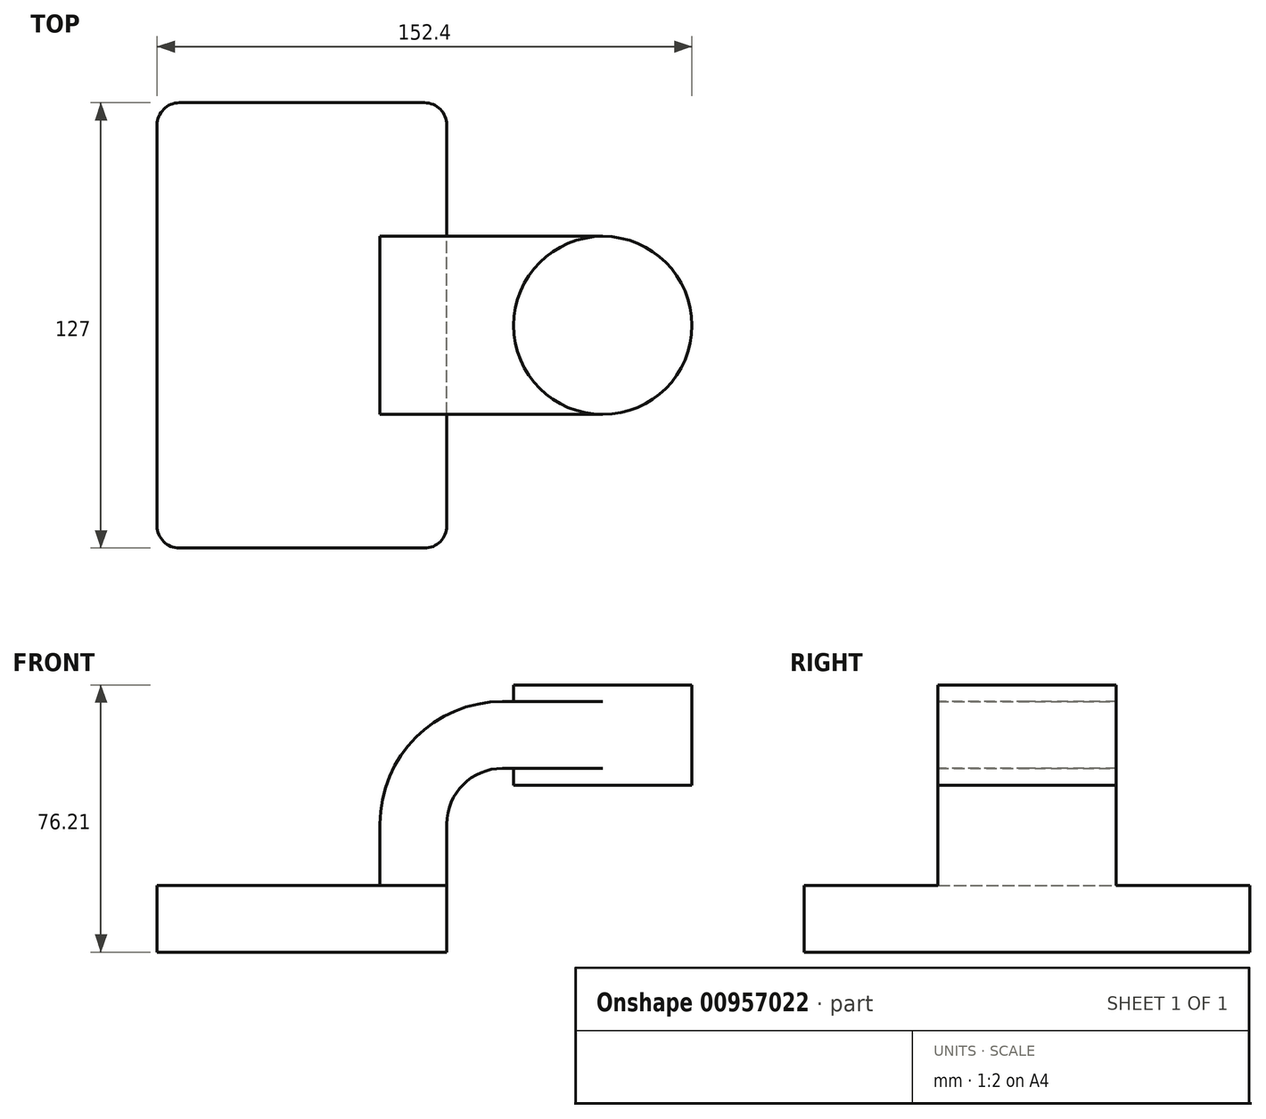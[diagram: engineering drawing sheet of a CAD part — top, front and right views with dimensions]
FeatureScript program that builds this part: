
annotation { "Feature Type Name" : "Feature", "Feature Type Description" : "" }
export const myFeature = defineFeature(function(context is Context, id is Id, definition is map)
    precondition{}
    {
        {
            var Q0;
            Q0=qCreatedBy(makeId("Front.planeOp"),FACE);
            var sketch = newSketch(context, id + "F0", { "sketchPlane" : qUnion([Q0])});
            skLineSegment(sketch, "E0.bottom", {"start": v(41.27, 9.52) * mm, "end": v(-41.28, 9.52) * mm});
            skLineSegment(sketch, "E0.top", {"start": v(41.28, -9.53) * mm, "end": v(-41.27, -9.53) * mm});
            skLineSegment(sketch, "E0.left", {"start": v(41.28, 9.53) * mm, "end": v(41.28, -9.52) * mm});
            skLineSegment(sketch, "E0.right", {"start": v(-41.27, 9.53) * mm, "end": v(-41.27, -9.52) * mm});
            skPoint(sketch, "E0.middle", {"position": v(0, 0) * mm});
            skLineSegment(sketch, "E1.bottom", {"start": v(111.12, 38.1) * mm, "end": v(60.32, 38.1) * mm});
            skLineSegment(sketch, "E1.top", {"start": v(111.12, 66.68) * mm, "end": v(60.33, 66.68) * mm});
            skLineSegment(sketch, "E1.left", {"start": v(111.12, 38.1) * mm, "end": v(111.12, 66.68) * mm});
            skLineSegment(sketch, "E1.right", {"start": v(60.32, 38.1) * mm, "end": v(60.32, 66.68) * mm});
            skPoint(sketch, "E1.middle", {"position": v(85.72, 52.39) * mm});
            skLineSegment(sketch, "E2", {"start": v(41.28, 9.53) * mm, "end": v(41.28, 27) * mm});
            skArc(sketch, "E3", {"start": v(41.27, 27) * mm, "mid": v(45.92, 38.23) * mm, "end": v(57.15, 42.88) * mm});
            skLineSegment(sketch, "E4", {"start": v(57.15, 42.88) * mm, "end": v(85.72, 42.88) * mm});
            skLineSegment(sketch, "E5.0", {"start": v(57.15, 61.93) * mm, "end": v(85.72, 61.93) * mm});
            skArc(sketch, "E5.1", {"start": v(22.23, 27) * mm, "mid": v(32.45, 51.7) * mm, "end": v(57.15, 61.93) * mm});
            skLineSegment(sketch, "E5.2", {"start": v(22.22, 9.53) * mm, "end": v(22.22, 27) * mm});
            skFitSpline(sketch, "E6", {"points": [v(-41.27, 9.53) * mm, v(57.15, 61.93) * mm], "startDerivative": vector(2.15, 157.2) * mm, "endDerivative": vector(50.04, 0) * mm});
            skLineSegment(sketch, "E7", {"start": v(85.72, 38.1) * mm, "end": v(85.72, 66.68) * mm});
            skSolve(sketch);
        }
        {
            var Q0;
            Q0=makeQuery(id+"F0.imprint","IMPRINT",FACE,{"disambiguationData":[TD([[makeQuery(id+"F0.imprint","IMPRINT",EDGE,{"derivedFrom":sQuery(id+"F0.wireOp",EDGE,"E0.top")}),-1.0]])]});
            extrude(context, id + "F1", {"entities" : qUnion([Q0]), "endBound" : BoundingType.SYMMETRIC, "depth" : 127 * mm, "offsetDistance" : 25.4 * mm});
        }
        {
            var Q0;
            {var subQ1=sQuery(id+"F0.wireOp",EDGE,"E2");Q0=makeQuery(id+"F0.imprint","IMPRINT",FACE,{"disambiguationData":[TD([[makeQuery(id+"F0.imprint","IMPRINT",EDGE,{"derivedFrom":subQ1}),1.0]])]});}
            var Q1;
            {var subQ0=sQuery(id+"F0.wireOp",EDGE,"E4");var subQ1=sQuery(id+"F0.wireOp",EDGE,"E1.right");var subQ2=makeQuery(id+"F0.imprint","INTERSECT",VERTEX,{"derivedFrom":[subQ1,subQ0]});Q1=makeQuery(id+"F0.imprint","IMPRINT",FACE,{"disambiguationData":[TD([[makeQuery(id+"F0.imprint","IMPRINT",EDGE,{"disambiguationData":[TD([[subQ2,-1.0]])],"derivedFrom":subQ1}),-1.0]])]});}
            extrude(context, id + "F2", {"entities" : qUnion([Q0, Q1]), "operationType" : NewBodyOperationType.ADD, "endBound" : BoundingType.SYMMETRIC, "depth" : 50.8 * mm, "offsetDistance" : 25.4 * mm});
        }
        {
            var Q0;
            Q0=makeQuery(id+"F0.imprint","IMPRINT",FACE,{"disambiguationData":[TD([[makeQuery(id+"F0.imprint","IMPRINT",EDGE,{"derivedFrom":sQuery(id+"F0.wireOp",EDGE,"E5.1")}),1.0]])]});
            extrude(context, id + "F3", {"entities" : qUnion([Q0]), "operationType" : NewBodyOperationType.ADD, "endBound" : BoundingType.SYMMETRIC, "depth" : 15.88 * mm, "offsetDistance" : 25.4 * mm});
        }
        {
            var Q0;
            {var subQ0=sQuery(id+"F0.wireOp",EDGE,"E1.left");Q0=makeQuery(id+"F0.imprint","IMPRINT",FACE,{"disambiguationData":[TD([[makeQuery(id+"F0.imprint","IMPRINT",EDGE,{"derivedFrom":subQ0}),1.0]])]});}
            var Q1;
            Q1=sQuery(id+"F0.wireOp",EDGE,"E7");
            revolve(context, id + "F4", {"operationType" : NewBodyOperationType.ADD, "surfaceOperationType" : NewSurfaceOperationType.NEW, "entities" : qUnion([Q0]), "axis" : qUnion([Q1]), "revolveType" : RevolveType.FULL});
        }
        {
            var Q0;
            Q0=makeQuery(id+"F1.opExtrude","CAP_EDGE",EDGE,{"disambiguationData":[OSD([sQuery(id+"F0.wireOp",EDGE,"E0.right")])],"isStart":false});
            var Q1;
            Q1=makeQuery(id+"F1.opExtrude","CAP_EDGE",EDGE,{"disambiguationData":[OSD([sQuery(id+"F0.wireOp",EDGE,"E0.left")])],"isStart":false});
            var Q2;
            Q2=makeQuery(id+"F1.opExtrude","CAP_EDGE",EDGE,{"disambiguationData":[OSD([sQuery(id+"F0.wireOp",EDGE,"E0.left")])],"isStart":true});
            var Q3;
            Q3=makeQuery(id+"F1.opExtrude","CAP_EDGE",EDGE,{"disambiguationData":[OSD([sQuery(id+"F0.wireOp",EDGE,"E0.right")])],"isStart":true});
            fillet(context, id + "F5", {"entities" : qUnion([Q0, Q1, Q2, Q3]), "radius" : 6.35 * mm, "tangentPropagation" : true, "allowEdgeOverflow" : false});
        }
    });
